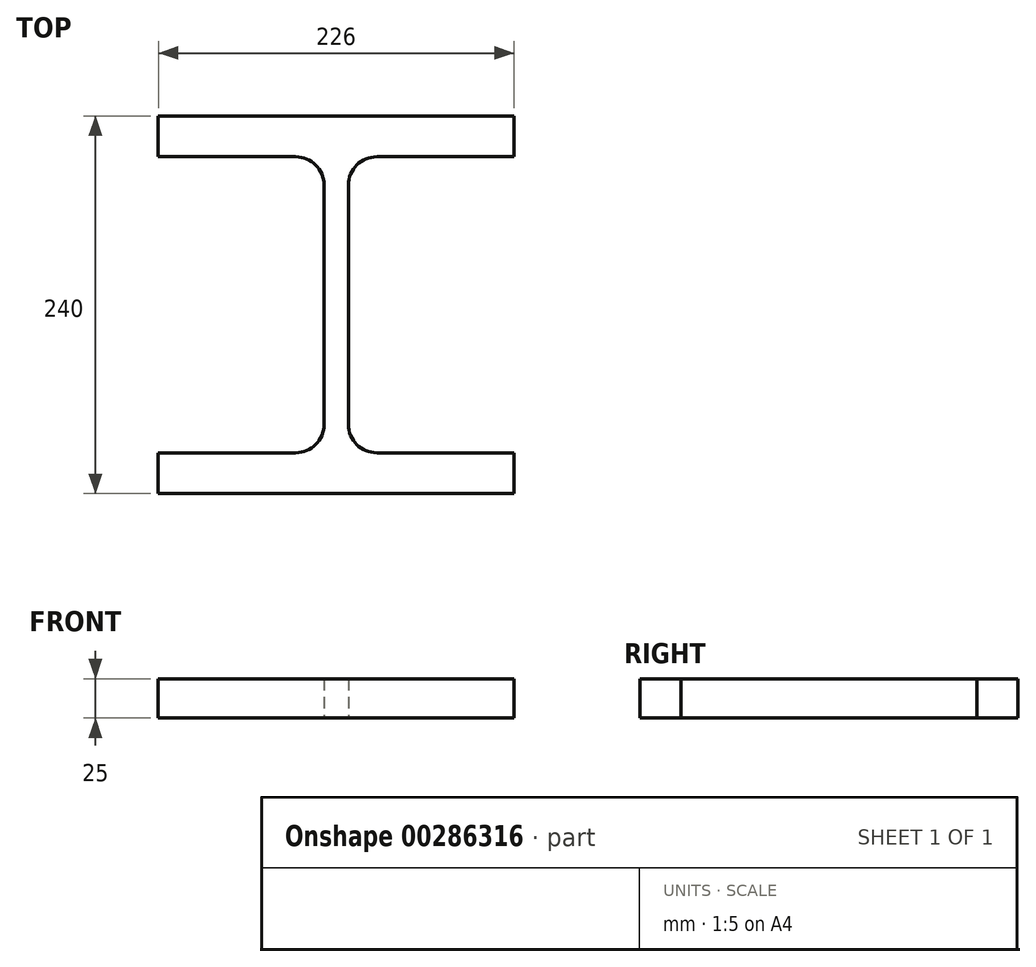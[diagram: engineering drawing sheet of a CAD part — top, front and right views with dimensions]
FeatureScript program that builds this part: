
annotation { "Feature Type Name" : "Feature", "Feature Type Description" : "" }
export const myFeature = defineFeature(function(context is Context, id is Id, definition is map)
    precondition{}
    {
        {
            var Q0;
            Q0=qCreatedBy(makeId("Top.planeOp"),FACE);
            var sketch = newSketch(context, id + "F0", { "sketchPlane" : qUnion([Q0])});
            skLineSegment(sketch, "E0", {"start": v(-58.75, 176.86) * mm, "end": v(-58.75, 150.86) * mm});
            skLineSegment(sketch, "E1", {"start": v(-58.75, -37.14) * mm, "end": v(-58.75, -63.14) * mm});
            skLineSegment(sketch, "E2", {"start": v(54.25, 176.86) * mm, "end": v(54.25, 140.49) * mm, "construction": true});
            skLineSegment(sketch, "E3", {"start": v(167.25, -63.14) * mm, "end": v(167.25, -37.14) * mm});
            skLineSegment(sketch, "E4", {"start": v(-58.75, 150.86) * mm, "end": v(28.5, 150.86) * mm});
            skLineSegment(sketch, "E5", {"start": v(-58.75, -37.14) * mm, "end": v(28.5, -37.14) * mm});
            skPoint(sketch, "E6.start.orphan", {"position": v(54.25, 140.49) * mm});
            skPoint(sketch, "E7.endSnap0", {"position": v(54.25, 150.86) * mm});
            skLineSegment(sketch, "E8.trimOffspring", {"start": v(80, -37.14) * mm, "end": v(167.25, -37.14) * mm});
            skLineSegment(sketch, "E9.trimOffspring", {"start": v(80, 150.86) * mm, "end": v(167.25, 150.86) * mm});
            skLineSegment(sketch, "E10.trimOffspring", {"start": v(167.25, 150.86) * mm, "end": v(167.25, 176.86) * mm});
            skLineSegment(sketch, "E11", {"start": v(46.5, 132.86) * mm, "end": v(46.5, -19.14) * mm});
            skLineSegment(sketch, "E12", {"start": v(62, 132.86) * mm, "end": v(62, -19.14) * mm});
            skPoint(sketch, "E13.visualSharp", {"position": v(46.5, 150.86) * mm});
            skArc(sketch, "E13.filletArc", {"start": v(46.5, 132.86) * mm, "mid": v(41.22, 145.58) * mm, "end": v(28.5, 150.86) * mm});
            skPoint(sketch, "E14.visualSharp", {"position": v(62, 150.86) * mm});
            skArc(sketch, "E14.filletArc", {"start": v(80, 150.86) * mm, "mid": v(67.27, 145.58) * mm, "end": v(62, 132.86) * mm});
            skPoint(sketch, "E15.visualSharp", {"position": v(62, -37.14) * mm});
            skArc(sketch, "E15.filletArc", {"start": v(62, -19.14) * mm, "mid": v(67.27, -31.87) * mm, "end": v(80, -37.14) * mm});
            skPoint(sketch, "E16.start.orphan", {"position": v(54.25, -63.14) * mm});
            skLineSegment(sketch, "E17", {"start": v(-58.75, 176.86) * mm, "end": v(167.25, 176.86) * mm});
            skLineSegment(sketch, "E18", {"start": v(-58.75, -63.14) * mm, "end": v(167.25, -63.14) * mm});
            skPoint(sketch, "E19.visualSharp", {"position": v(46.5, -37.14) * mm});
            skArc(sketch, "E19.filletArc", {"start": v(28.5, -37.14) * mm, "mid": v(41.22, -31.87) * mm, "end": v(46.5, -19.14) * mm});
            skSolve(sketch);
        }
        {
            var Q0;
            Q0 = qSketchRegion(id + "F0", true);
            var Q1;
            Q1=makeQuery(id+"F0.imprint","IMPRINT",FACE,{"disambiguationData":[TD([[makeQuery(id+"F0.imprint","IMPRINT",EDGE,{"derivedFrom":sQuery(id+"F0.wireOp",EDGE,"E0")}),1.0]])]});
            extrude(context, id + "F1", {"entities" : qUnion([Q0, Q1]), "depth" : 25 * mm});
        }
    });
